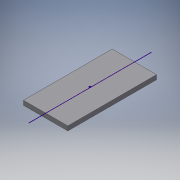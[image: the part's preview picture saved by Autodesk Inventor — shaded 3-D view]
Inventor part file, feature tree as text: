
AUTODESK INVENTOR PART (.ipt)
format: ipt  version: 2019 (Build 230136000, 136)  size: 96,256 bytes
history: native  units: in
note: dims shown in document units (in); Inventor stores cm internally (conversion verified against a paired STEP export)
features: extrude x1, sketch x1
ambient origin geometry x8: Origin, YZ Plane, XZ Plane, XY Plane, X Axis, Y Axis, Z Axis, Center Point
bodies: Solid1 (feature_tree)
feature tree (2):
  extrude  "Extrusion1"  Depth=0.1969in
  sketch  "Sketch1"  dims[d0=0.3937in d1=0.1969in d2=0.0197in d3=0.0in]
